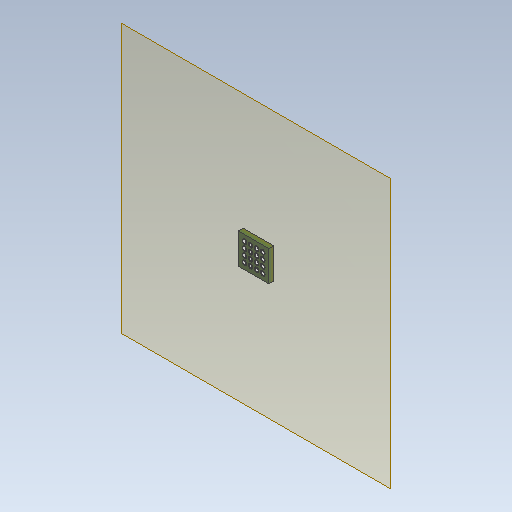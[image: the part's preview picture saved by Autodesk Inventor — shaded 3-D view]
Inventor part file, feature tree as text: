
AUTODESK INVENTOR PART (.ipt)
format: ipt  version: 2021 (Build 250183000, 183)  size: 209,408 bytes
history: native  units: in
note: dims shown in document units (in); Inventor stores cm internally (conversion verified against a paired STEP export)
features: other x3, sketch x3, plane x1
ambient origin geometry x8: Origin, YZ Plane, XZ Plane, XY Plane, X Axis, Y Axis, Z Axis, Center Point
bodies: Solid1 (feature_tree)
feature tree (7):
  other  "1.27mmpitchProtoboardDesign.ipt_.25inch_.25Inch.ipt"
  other  "Solid1::1.27mmpitchProtoboardDesign.ipt_.25inch_.25Inch.ipt"
  other  "TaggingFeature1"
  sketch  "Sketch1"  dims[d0=0.3937in]
  sketch  "Sketch2"  dims[d1=0.12in]
  sketch  "Sketch3"
  plane  "Work Plane1"
